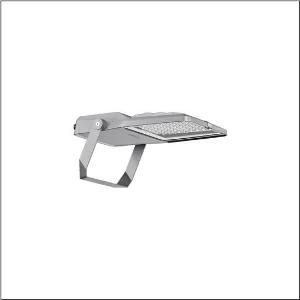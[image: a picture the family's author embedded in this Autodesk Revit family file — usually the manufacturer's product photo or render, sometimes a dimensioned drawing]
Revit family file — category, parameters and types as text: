
# Revit family: floodlight_fl_21_iq_mini___rs12_5xa7772b5b1a_54c6
name_source: partatom
category: Lighting Fixtures
units: mm (PartAtom-declared; Revit-internal decimal feet)

## family parameters
Cut with Voids When Loaded = No
Host = Face
Light Source = No
Part Type = Normal
Room Calculation Point = No
Round Connector Dimension = Use Diameter
Shared = No

## types (1)
- --- (1 x LED, 5880 lm, 45.5 W, 4000K)
    Apparent Load = 46 VA
    CIE Flux Codes = 79 92 99 100 100
    Color Rendering = 80
    Color Temperature = 4000K
    Default Elevation = 1800 mm
    Description = Floodlight FL 21 iQ mini, floodlight, primary light control with lens, of PMMA, primary optical cover: protective disc, of toughened safety glass, transparent, light distribution: RS12, light emission: direct distribution, installation type: surface-mounted, lamps: LED, High Power LED, rated values: 5.880lm | 45,5W | 129,2lm/W (begin service life); end service life: 5.880lm | 48W; at 50% lumin. flux: 2.940lm | 21,5W | 136,7lm/W, colour temperature: 4000K, colour rendering: CRI > 80, light colour: 840, light setting 1 begin service life: 100% | 5.880lm | 45,5W | 129,2lm/W | 4.000K, light setting 1 end service life: 48W, further light settings possible, control: Street-Remote, Auto-Match, Temp-Guard, Night-Set, Smart-Wire, Desk-Remote (wireless, voltage-free reading and setting of iQ features in the workshop via application-optimized NFC function/RFID function), optimised constant luminous flux control (CLO 2.0), pre-setting: linear dimming characteristic, with terminal, 6-pole, mains connection: 220..240V, AC, 50/60Hz, luminaire housing, of diecast aluminium, powder-coated, SITECO metallic grey (DB 702S), corrosivity category C5 mid according to DIN EN ISO 12944suitable for swimming poolschlorine-resistant, sealing non-destructively replaceable, mounting bracket, of steel, galvanised, powder-coated, SITECO metallic grey (DB 702S), protection rating (complete): IP66, insulation class (complete): insulation class II (safety insulation), certification: CE, ENEC, VDE, protection symbol: D, impact resistance: IK08, permissible operating ambient temperature: -40..+40°C, permissible operating ambient temperature for outdoor applications: -40..+50°C, standard: DIN EN 12944, LABS conformity tested according to VDMA 24364:2018-05, packaging unit: 1 piece

Light Distribution: RS12
    Height = 70 mm
    Lamp = 1 x LED
    Lamp Light Flux = 5880 lm
    Lamp Power = 45.5 W
    Lamp count = 1
    Length = 485 mm
    Luminous efficacy = 129 lm/W
    Manufacturer = Siteco
    ModVariant = No
    Model = 5XA7772B5B1A
    Mounting Place = Pole
    Mounting Type = Pole annexe
    Number of Poles = 1
    OnlyDefault = Yes
    Power Factor = 1
    Product Name = Floodlight FL 21 iQ mini | RS12
    Product group = floodlight | pylon annexe
    ProductGroupID = 6201
    Protection Class = Protection class II
    Protection Degree = IP 66
    RLX_Detail_Level = 1
    RLX_Emergency_Light_Flux = 0 lm
    RLX_Emergency_Type = 0
    RLX_Emergency_Type_DB = No
    RlxData = <blob elided: 91101 chars, md5=77edeea3>
    Socket = socket
    Standby Power = 0 W
    System Light Flux = 5880 lm
    System Power = 46 W
    Type Comments = factory setting: luminous flux: 100 % | dim-lin: 254 | 463 mA
    Type Image = l_1006845.jpg
    URL = http://relux.com
    VarID = @adj_168813
    Voltage = 0 V
    Weight = 0.00 kg
    Width = 337 mm

## geometry (parser evidence)
native form markers: Blend x4, Sweep x12
no freeform markers — native parametric forms only
